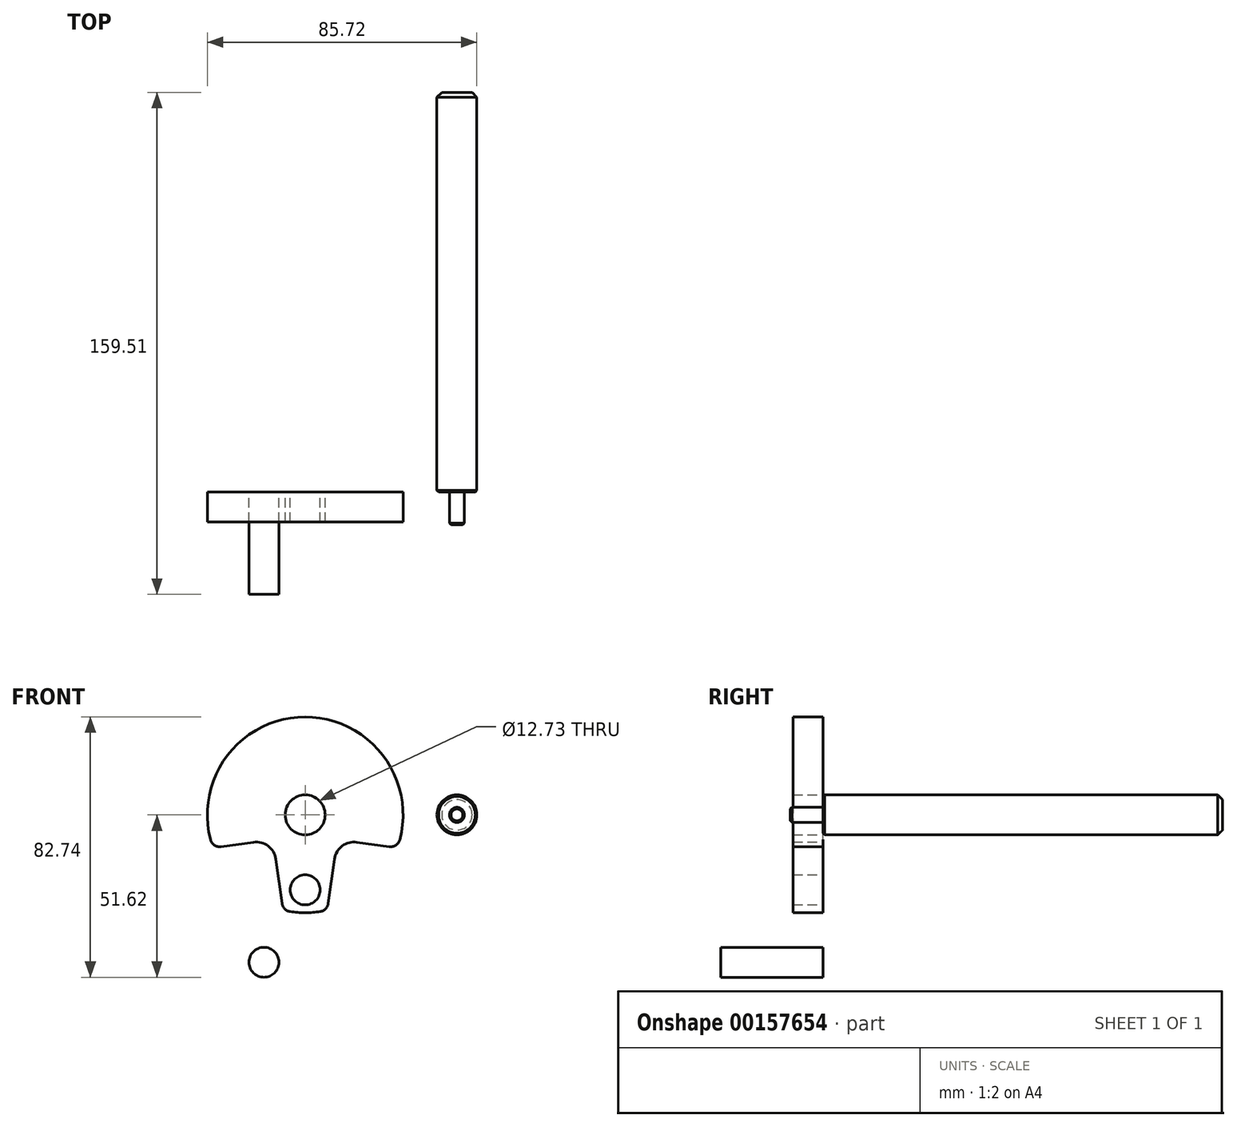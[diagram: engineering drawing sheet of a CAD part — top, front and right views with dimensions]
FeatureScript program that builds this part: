
annotation { "Feature Type Name" : "Feature", "Feature Type Description" : "" }
export const myFeature = defineFeature(function(context is Context, id is Id, definition is map)
    precondition{}
    {
        {
            var Q0;
            Q0=qCreatedBy(makeId("Front.planeOp"),FACE);
            var sketch = newSketch(context, id + "F0", { "sketchPlane" : qUnion([Q0])});
            skCircle(sketch, "E0", {"center": v(0, 0) * mm, "radius": 6.35 * mm});
            skSolve(sketch);
        }
        {
            var Q0;
            Q0=makeQuery(id+"F0.imprint","IMPRINT",FACE,{"disambiguationData":[TD([[makeQuery(id+"F0.imprint","IMPRINT",EDGE,{"derivedFrom":sQuery(id+"F0.wireOp",EDGE,"E0")}),1.0]])]});
            extrude(context, id + "F1", {"entities" : qUnion([Q0]), "oppositeDirection" : true, "depth" : 127 * mm});
        }
        {
            var Q0;
            Q0=makeQuery(id+"F1.opExtrude","CAP_FACE",FACE,{"disambiguationData":[OSD([sQuery(id+"F0.wireOp",EDGE,"E0")])],"isStart":true});
            var sketch = newSketch(context, id + "F2", { "sketchPlane" : qUnion([Q0])});
            skCircle(sketch, "E1", {"center": v(0, 0) * mm, "radius": 2.38 * mm});
            skSolve(sketch);
        }
        {
            var Q0;
            Q0=makeQuery(id+"F2.imprint","IMPRINT",FACE,{"disambiguationData":[TD([[makeQuery(id+"F2.imprint","IMPRINT",EDGE,{"derivedFrom":sQuery(id+"F2.wireOp",EDGE,"E1")}),1.0]])]});
            extrude(context, id + "F3", {"entities" : qUnion([Q0]), "operationType" : NewBodyOperationType.ADD, "depth" : 10.4 * mm});
        }
        {
            var Q0;
            Q0=makeQuery(id+"F3.opExtrude","CAP_EDGE",EDGE,{"disambiguationData":[OSD([sQuery(id+"F2.wireOp",EDGE,"E1")])],"isStart":false});
            var Q1;
            Q1=makeQuery(id+"F1.opExtrude","CAP_EDGE",EDGE,{"disambiguationData":[OSD([sQuery(id+"F0.wireOp",EDGE,"E0")])],"isStart":true});
            chamfer(context, id + "F4", {"entities" : qUnion([Q0, Q1]), "width" : 0.5 * mm, "tangentPropagation" : true});
        }
        {
            var Q0;
            Q0=makeQuery(id+"F1.opExtrude","CAP_EDGE",EDGE,{"disambiguationData":[OSD([sQuery(id+"F0.wireOp",EDGE,"E0")])],"isStart":false});
            chamfer(context, id + "F5", {"entities" : qUnion([Q0]), "width" : 1.52 * mm, "tangentPropagation" : true});
        }
        {
            var Q0;
            Q0=qCreatedBy(makeId("Front.planeOp"),FACE);
            var sketch = newSketch(context, id + "F6", { "sketchPlane" : qUnion([Q0])});
            skArc(sketch, "E2", {"start": v(-18.15, -7.87) * mm, "mid": v(-48.25, 31.12) * mm, "end": v(-78.35, -7.87) * mm});
            skLineSegment(sketch, "E3", {"start": v(-48.25, 0) * mm, "end": v(-48.25, -40.8) * mm, "construction": true});
            skCircle(sketch, "E4", {"center": v(-48.25, -23.83) * mm, "radius": 4.78 * mm});
            skCircle(sketch, "E5", {"center": v(-48.25, 0) * mm, "radius": 6.36 * mm});
            skArc(sketch, "E6", {"start": v(-40.45, -24.92) * mm, "mid": v(-48.25, -15.95) * mm, "end": v(-56.05, -24.92) * mm, "construction": true});
            skLineSegment(sketch, "E7", {"start": v(-48.25, -23.83) * mm, "end": v(-51.49, -23.83) * mm, "construction": true});
            skLineSegment(sketch, "E8", {"start": v(-48.25, -23.83) * mm, "end": v(-56.05, -24.92) * mm, "construction": true});
            skLineSegment(sketch, "E9", {"start": v(-56.05, -24.92) * mm, "end": v(-57.57, -14.08) * mm});
            skLineSegment(sketch, "E10", {"start": v(-64.74, -8.68) * mm, "end": v(-74.98, -10.12) * mm});
            skLineSegment(sketch, "E11", {"start": v(-56.05, -24.92) * mm, "end": v(-55.6, -28.16) * mm});
            skLineSegment(sketch, "E12", {"start": v(-48.25, -23.83) * mm, "end": v(-40.45, -24.92) * mm, "construction": true});
            skLineSegment(sketch, "E13", {"start": v(-40.45, -24.92) * mm, "end": v(-38.93, -14.08) * mm});
            skLineSegment(sketch, "E14", {"start": v(-40.45, -24.92) * mm, "end": v(-40.9, -28.16) * mm});
            skArc(sketch, "E15.trimOffspring", {"start": v(-53.05, -30.74) * mm, "mid": v(-48.25, -31.12) * mm, "end": v(-43.46, -30.74) * mm});
            skLineSegment(sketch, "E16", {"start": v(-31.76, -8.68) * mm, "end": v(-21.52, -10.12) * mm});
            skArc(sketch, "E17.filletArc", {"start": v(-57.57, -14.08) * mm, "mid": v(-60.04, -9.9) * mm, "end": v(-64.74, -8.68) * mm});
            skArc(sketch, "E18.filletArc", {"start": v(-31.76, -8.68) * mm, "mid": v(-36.46, -9.9) * mm, "end": v(-38.93, -14.08) * mm});
            skArc(sketch, "E19.filletArc", {"start": v(-43.46, -30.74) * mm, "mid": v(-41.76, -29.87) * mm, "end": v(-40.9, -28.16) * mm});
            skArc(sketch, "E20.filletArc", {"start": v(-55.6, -28.16) * mm, "mid": v(-54.75, -29.87) * mm, "end": v(-53.05, -30.74) * mm});
            skArc(sketch, "E21.filletArc", {"start": v(-21.52, -10.12) * mm, "mid": v(-19.4, -9.64) * mm, "end": v(-18.15, -7.87) * mm});
            skArc(sketch, "E22.filletArc", {"start": v(-78.35, -7.87) * mm, "mid": v(-77.1, -9.64) * mm, "end": v(-74.98, -10.12) * mm});
            skSolve(sketch);
        }
        {
            var Q0;
            Q0=makeQuery(id+"F6.imprint","IMPRINT",FACE,{"disambiguationData":[TD([[makeQuery(id+"F6.imprint","IMPRINT",EDGE,{"derivedFrom":sQuery(id+"F6.wireOp",EDGE,"E2")}),1.0]])]});
            extrude(context, id + "F7", {"entities" : qUnion([Q0]), "depth" : 9.52 * mm});
        }
        {
            var Q0;
            Q0=qCreatedBy(makeId("Front.planeOp"),FACE);
            var sketch = newSketch(context, id + "F8", { "sketchPlane" : qUnion([Q0])});
            skCircle(sketch, "E23", {"center": v(-61.35, -46.86) * mm, "radius": 4.76 * mm});
            skSolve(sketch);
        }
        {
            var Q0;
            Q0=makeQuery(id+"F8.imprint","IMPRINT",FACE,{"disambiguationData":[TD([[makeQuery(id+"F8.imprint","IMPRINT",EDGE,{"derivedFrom":sQuery(id+"F8.wireOp",EDGE,"E23")}),1.0]])]});
            extrude(context, id + "F9", {"entities" : qUnion([Q0]), "depth" : 32.5 * mm});
        }
    });
